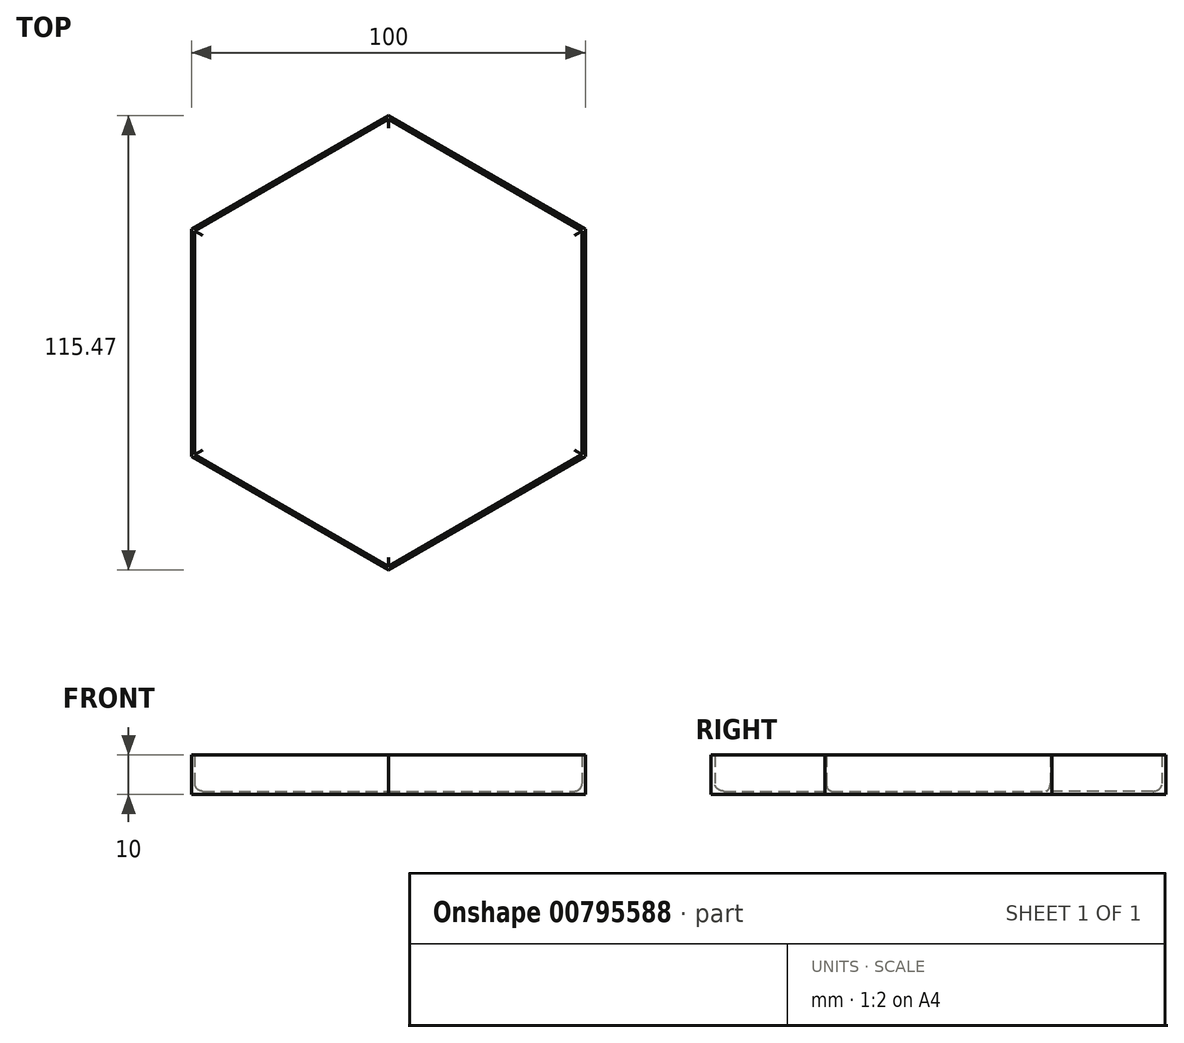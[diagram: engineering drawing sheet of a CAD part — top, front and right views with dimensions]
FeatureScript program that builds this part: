
annotation { "Feature Type Name" : "Feature", "Feature Type Description" : "" }
export const myFeature = defineFeature(function(context is Context, id is Id, definition is map)
    precondition{}
    {
        {
            var Q0;
            Q0=qCreatedBy(makeId("Top.planeOp"),FACE);
            var sketch = newSketch(context, id + "F0", { "sketchPlane" : qUnion([Q0])});
            skLineSegment(sketch, "E0", {"start": v(3.46, -52.58) * mm, "end": v(3.46, 60.42) * mm, "construction": true});
            skLineSegment(sketch, "E1", {"start": v(-32.16, -19.02) * mm, "end": v(3.46, 1.54) * mm, "construction": true});
            skLineSegment(sketch, "E2", {"start": v(3.46, 1.54) * mm, "end": v(46.96, 26.66) * mm, "construction": true});
            skLineSegment(sketch, "E3", {"start": v(3.46, 1.54) * mm, "end": v(49.93, -25.28) * mm, "construction": true});
            skLineSegment(sketch, "E4", {"start": v(3.46, 1.54) * mm, "end": v(-48.3, 31.42) * mm, "construction": true});
            skLineSegment(sketch, "E5", {"start": v(3.46, 59.28) * mm, "end": v(53.46, 30.41) * mm});
            skLineSegment(sketch, "E6", {"start": v(53.46, 30.41) * mm, "end": v(53.46, -27.32) * mm});
            skLineSegment(sketch, "E7", {"start": v(53.46, -27.32) * mm, "end": v(3.46, -56.2) * mm});
            skLineSegment(sketch, "E8", {"start": v(3.46, -56.2) * mm, "end": v(-46.54, -27.32) * mm});
            skLineSegment(sketch, "E9", {"start": v(-46.54, -27.32) * mm, "end": v(-46.54, 30.41) * mm});
            skLineSegment(sketch, "E10", {"start": v(-46.54, 30.41) * mm, "end": v(3.46, 59.28) * mm});
            skLineSegment(sketch, "E11", {"start": v(-46.54, -27.32) * mm, "end": v(-32.16, -19.02) * mm, "construction": true});
            skSolve(sketch);
        }
        {
            var Q0;
            Q0=makeQuery(id+"F0.imprint","IMPRINT",FACE,{"disambiguationData":[TD([[makeQuery(id+"F0.imprint","IMPRINT",EDGE,{"derivedFrom":sQuery(id+"F0.wireOp",EDGE,"E5")}),-1.0]])]});
            extrude(context, id + "F1", {"entities" : qUnion([Q0]), "depth" : 10 * mm, "offsetDistance" : 25 * mm});
        }
        {
            var Q0;
            Q0=makeQuery(id+"F1.opExtrude","CAP_FACE",FACE,{"disambiguationData":[OSD([sQuery(id+"F0.wireOp",EDGE,"E5"),sQuery(id+"F0.wireOp",EDGE,"E6"),sQuery(id+"F0.wireOp",EDGE,"E7"),sQuery(id+"F0.wireOp",EDGE,"E8"),sQuery(id+"F0.wireOp",EDGE,"E9"),sQuery(id+"F0.wireOp",EDGE,"E10")])],"isStart":false});
            shell(context, id + "F2", {"entities" : qUnion([Q0]), "thickness" : 0.8 * mm});
        }
        {
            var Q0;
            Q0=makeQuery(id+"F2.opShell","OFFSET_FACE",FACE,{"disambiguationData":[OSD([sQuery(id+"F0.wireOp",EDGE,"E5"),sQuery(id+"F0.wireOp",EDGE,"E6"),sQuery(id+"F0.wireOp",EDGE,"E7"),sQuery(id+"F0.wireOp",EDGE,"E8"),sQuery(id+"F0.wireOp",EDGE,"E9"),sQuery(id+"F0.wireOp",EDGE,"E10")])]});
            fillet(context, id + "F3", {"entities" : qUnion([Q0]), "radius" : 2 * mm, "tangentPropagation" : true, "allowEdgeOverflow" : false});
        }
    });
